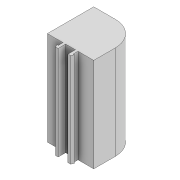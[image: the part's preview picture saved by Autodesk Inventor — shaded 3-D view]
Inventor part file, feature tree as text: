
AUTODESK INVENTOR PART (.ipt)
format: ipt  version: 2021 (Build 250183000, 183)  size: 126,976 bytes
history: native  units: mm
features: reference x10, extrude x3, sketch x3, other x2, direct_edit x1, move_body x1
ambient origin geometry x8: Origin, YZ Plane, XZ Plane, XY Plane, X Axis, Y Axis, Z Axis, Center Point
bodies: Volumenkörper1 (feature_tree)
feature tree (20):
  extrude  "Extrusion1"  Depth=20.0mm
  extrude  "Extrusion2"  TaperAngle=0.0deg  [1 undecoded]
  extrude  "Extrusion3"  Depth=10.0mm TaperAngle=0.0deg
  direct_edit  "Direktbearbeitung1"
  sketch  "Skizze1"  dims[d0=20.0mm d1=20.0mm]
  sketch  "Skizze2"  dims[d2=34.5mm d3=0.0mm d4=0.0mm d5=0.0mm]
  sketch  "Skizze3"  dims[d6=10.0mm d7=0.0mm d23=0.0mm d24=0.0mm d25=2.0mm]
  reference  "Referenz4"
  reference  "Referenz5"
  reference  "Referenz6"
  reference  "Referenz7"
  reference  "Referenz8"
  reference  "Referenz9"
  reference  "Referenz10"
  reference  "Referenz11"
  reference  "Referenz12"
  reference  "Referenz13"
  other  "Baugruppe2"
  other  "Light_Bar_Clip_-_Misumi (1):1"
  move_body  "Verschieben1"
note: 1 required parameter value undecoded (feature->parameter linkage not recoverable at this tier; creation-order binding heuristic only, values carry confidence <= 0.55)
